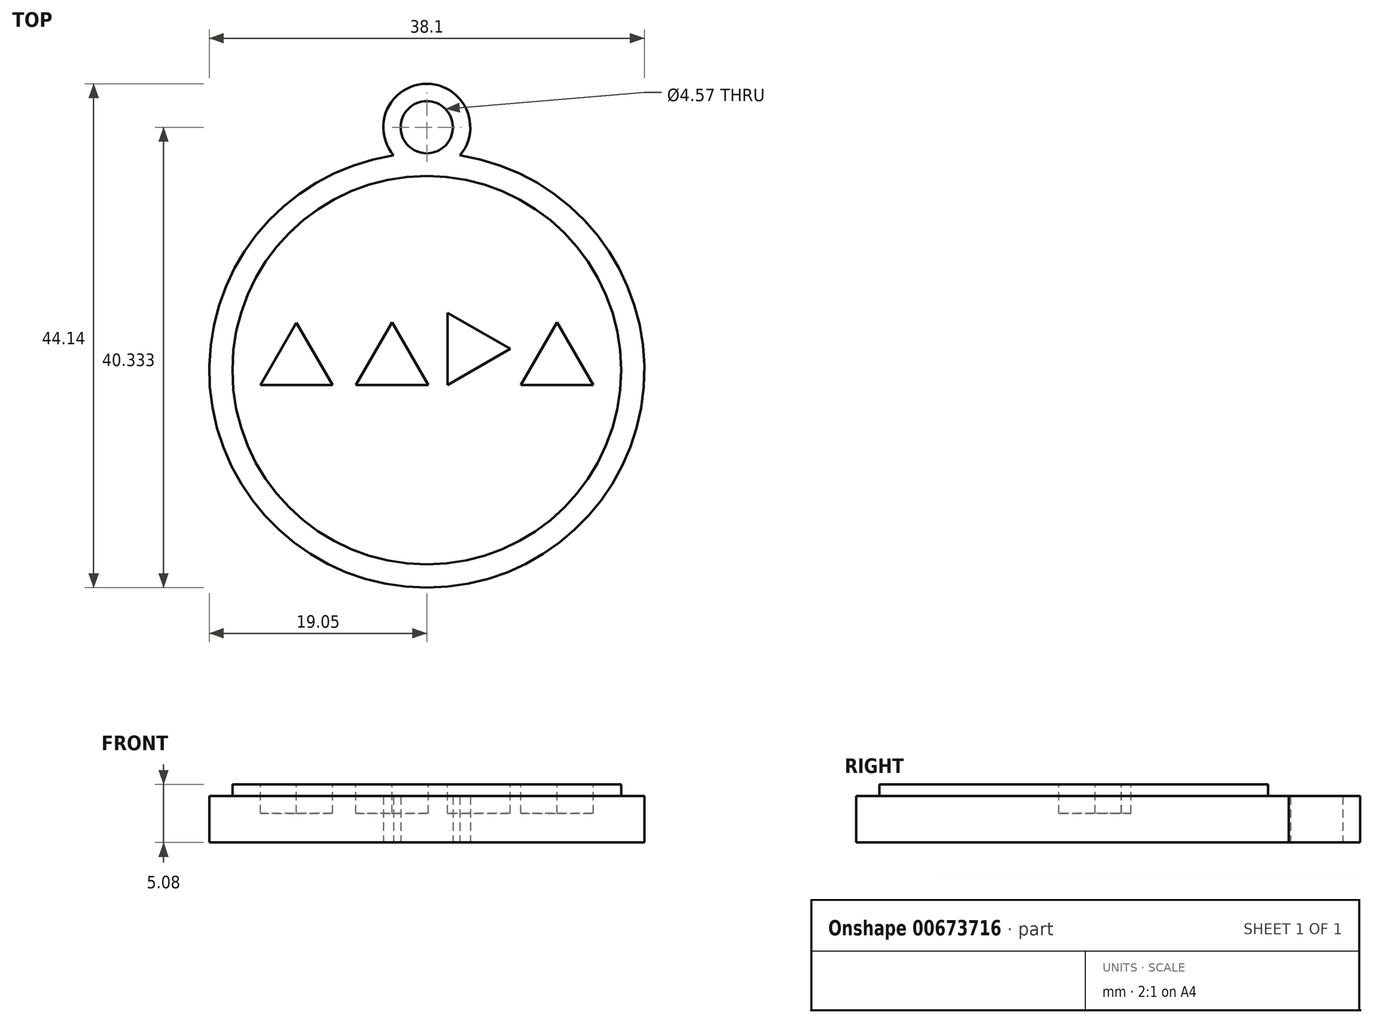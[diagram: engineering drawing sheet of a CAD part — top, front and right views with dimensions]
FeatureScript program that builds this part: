
annotation { "Feature Type Name" : "Feature", "Feature Type Description" : "" }
export const myFeature = defineFeature(function(context is Context, id is Id, definition is map)
    precondition{}
    {
        {
            var Q0;
            Q0=qCreatedBy(makeId("Top.planeOp"),FACE);
            var sketch = newSketch(context, id + "F0", { "sketchPlane" : qUnion([Q0])});
            skCircle(sketch, "E0", {"center": v(0, 30.05) * mm, "radius": 2.29 * mm});
            skArc(sketch, "E1", {"start": v(2.91, 27.6) * mm, "mid": v(0, 33.86) * mm, "end": v(-2.91, 27.6) * mm});
            skArc(sketch, "E2", {"start": v(-2.91, 27.6) * mm, "mid": v(0, -10.28) * mm, "end": v(2.91, 27.6) * mm});
            skCircle(sketch, "E3.0", {"center": v(0, 8.77) * mm, "radius": 17.02 * mm});
            skSolve(sketch);
        }
        {
            var Q0;
            Q0=makeQuery(id+"F0.imprint","IMPRINT",FACE,{"disambiguationData":[TD([[makeQuery(id+"F0.imprint","IMPRINT",EDGE,{"derivedFrom":sQuery(id+"F0.wireOp",EDGE,"E0")}),-1.0]])]});
            extrude(context, id + "F1", {"entities" : qUnion([Q0]), "depth" : 4.06 * mm, "offsetDistance" : 25.4 * mm});
        }
        {
            var Q0;
            Q0=makeQuery(id+"F0.imprint","IMPRINT",FACE,{"disambiguationData":[TD([[makeQuery(id+"F0.imprint","IMPRINT",EDGE,{"derivedFrom":sQuery(id+"F0.wireOp",EDGE,"E3.0")}),1.0]])]});
            extrude(context, id + "F2", {"entities" : qUnion([Q0]), "operationType" : NewBodyOperationType.ADD, "depth" : 5.08 * mm, "offsetDistance" : 25.4 * mm});
        }
        {
            var Q0;
            Q0=makeQuery(id+"F2.opExtrude","CAP_FACE",FACE,{"disambiguationData":[OSD([sQuery(id+"F0.wireOp",EDGE,"E3.0")])],"isStart":false});
            var sketch = newSketch(context, id + "F3", { "sketchPlane" : qUnion([Q0])});
            skCircle(sketch, "E4.cCircle", {"center": v(-11.4, 9.3) * mm, "radius": 1.83 * mm, "construction": true});
            skLineSegment(sketch, "E4.0", {"start": v(-11.41, 12.95) * mm, "end": v(-8.24, 7.46) * mm});
            skLineSegment(sketch, "E4.1", {"start": v(-8.24, 7.46) * mm, "end": v(-14.57, 7.46) * mm});
            skLineSegment(sketch, "E4.2", {"start": v(-14.57, 7.46) * mm, "end": v(-11.41, 12.95) * mm});
            skPoint(sketch, "E4.0.midPoint", {"position": v(-9.83, 10.2) * mm});
            skCircle(sketch, "E5.cCircle", {"center": v(-3.04, 9.3) * mm, "radius": 1.83 * mm, "construction": true});
            skLineSegment(sketch, "E5.0", {"start": v(-3.05, 12.95) * mm, "end": v(0.12, 7.47) * mm});
            skLineSegment(sketch, "E5.1", {"start": v(0.12, 7.47) * mm, "end": v(-6.2, 7.46) * mm});
            skLineSegment(sketch, "E5.2", {"start": v(-6.2, 7.46) * mm, "end": v(-3.05, 12.95) * mm});
            skPoint(sketch, "E5.0.midPoint", {"position": v(-1.46, 10.21) * mm});
            skCircle(sketch, "E6.cCircle", {"center": v(3.65, 10.64) * mm, "radius": 1.83 * mm, "construction": true});
            skLineSegment(sketch, "E6.0", {"start": v(7.3, 10.64) * mm, "end": v(1.82, 7.47) * mm});
            skLineSegment(sketch, "E6.1", {"start": v(1.82, 7.47) * mm, "end": v(1.82, 13.8) * mm});
            skLineSegment(sketch, "E6.2", {"start": v(1.82, 13.8) * mm, "end": v(7.3, 10.64) * mm});
            skPoint(sketch, "E6.0.midPoint", {"position": v(4.56, 9.06) * mm});
            skCircle(sketch, "E7.cCircle", {"center": v(11.4, 9.3) * mm, "radius": 1.83 * mm, "construction": true});
            skLineSegment(sketch, "E7.0", {"start": v(11.4, 12.96) * mm, "end": v(14.58, 7.48) * mm});
            skLineSegment(sketch, "E7.1", {"start": v(14.58, 7.48) * mm, "end": v(8.24, 7.47) * mm});
            skLineSegment(sketch, "E7.2", {"start": v(8.24, 7.47) * mm, "end": v(11.4, 12.96) * mm});
            skPoint(sketch, "E7.0.midPoint", {"position": v(13, 10.22) * mm});
            skSolve(sketch);
        }
        {
            var Q0;
            Q0=makeQuery(id+"F3.imprint","IMPRINT",FACE,{"disambiguationData":[TD([[makeQuery(id+"F3.imprint","IMPRINT",EDGE,{"derivedFrom":sQuery(id+"F3.wireOp",EDGE,"E4.0")}),-1.0]])]});
            var Q1;
            Q1=makeQuery(id+"F3.imprint","IMPRINT",FACE,{"disambiguationData":[TD([[makeQuery(id+"F3.imprint","IMPRINT",EDGE,{"derivedFrom":sQuery(id+"F3.wireOp",EDGE,"E5.0")}),-1.0]])]});
            var Q2;
            Q2=makeQuery(id+"F3.imprint","IMPRINT",FACE,{"disambiguationData":[TD([[makeQuery(id+"F3.imprint","IMPRINT",EDGE,{"derivedFrom":sQuery(id+"F3.wireOp",EDGE,"E6.0")}),-1.0]])]});
            var Q3;
            Q3=makeQuery(id+"F3.imprint","IMPRINT",FACE,{"disambiguationData":[TD([[makeQuery(id+"F3.imprint","IMPRINT",EDGE,{"derivedFrom":sQuery(id+"F3.wireOp",EDGE,"E7.0")}),-1.0]])]});
            extrude(context, id + "F4", {"entities" : qUnion([Q0, Q1, Q2, Q3]), "operationType" : NewBodyOperationType.REMOVE, "oppositeDirection" : true, "depth" : 2.54 * mm, "offsetDistance" : 25.4 * mm});
        }
    });
